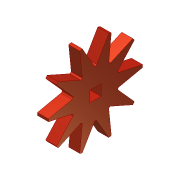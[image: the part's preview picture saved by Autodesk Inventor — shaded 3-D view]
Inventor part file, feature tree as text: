
AUTODESK INVENTOR PART (.ipt)
format: ipt  version: 2012 (Build 160160000, 160)  size: 125,440 bytes
history: native  units: in
note: dims shown in document units (in); Inventor stores cm internally (conversion verified against a paired STEP export)
features: extrude x2, sketch x2, pattern_circular x1
ambient origin geometry x8: Origin, YZ Plane, XZ Plane, XY Plane, X Axis, Y Axis, Z Axis, Center Point
bodies: Solid1 (feature_tree)
feature tree (5):
  extrude  "Extrusion1"  Depth=0.5in
  extrude  "Extrusion3"  Depth=0.2257in
  pattern_circular  "Circular Pattern2"  [2 undecoded]
  sketch  "Sketch1"  dims[d0=4.25in d1=0.5in]
  sketch  "Sketch2"  dims[d2=0.5in d3=0.0in d4=0.2257in d11=0.0625in d12=1.0in d13=1.0in d14=0.0in d15=3.937in d16=360.0deg]
note: 2 required parameter values undecoded (feature->parameter linkage not recoverable at this tier; creation-order binding heuristic only, values carry confidence <= 0.55)
